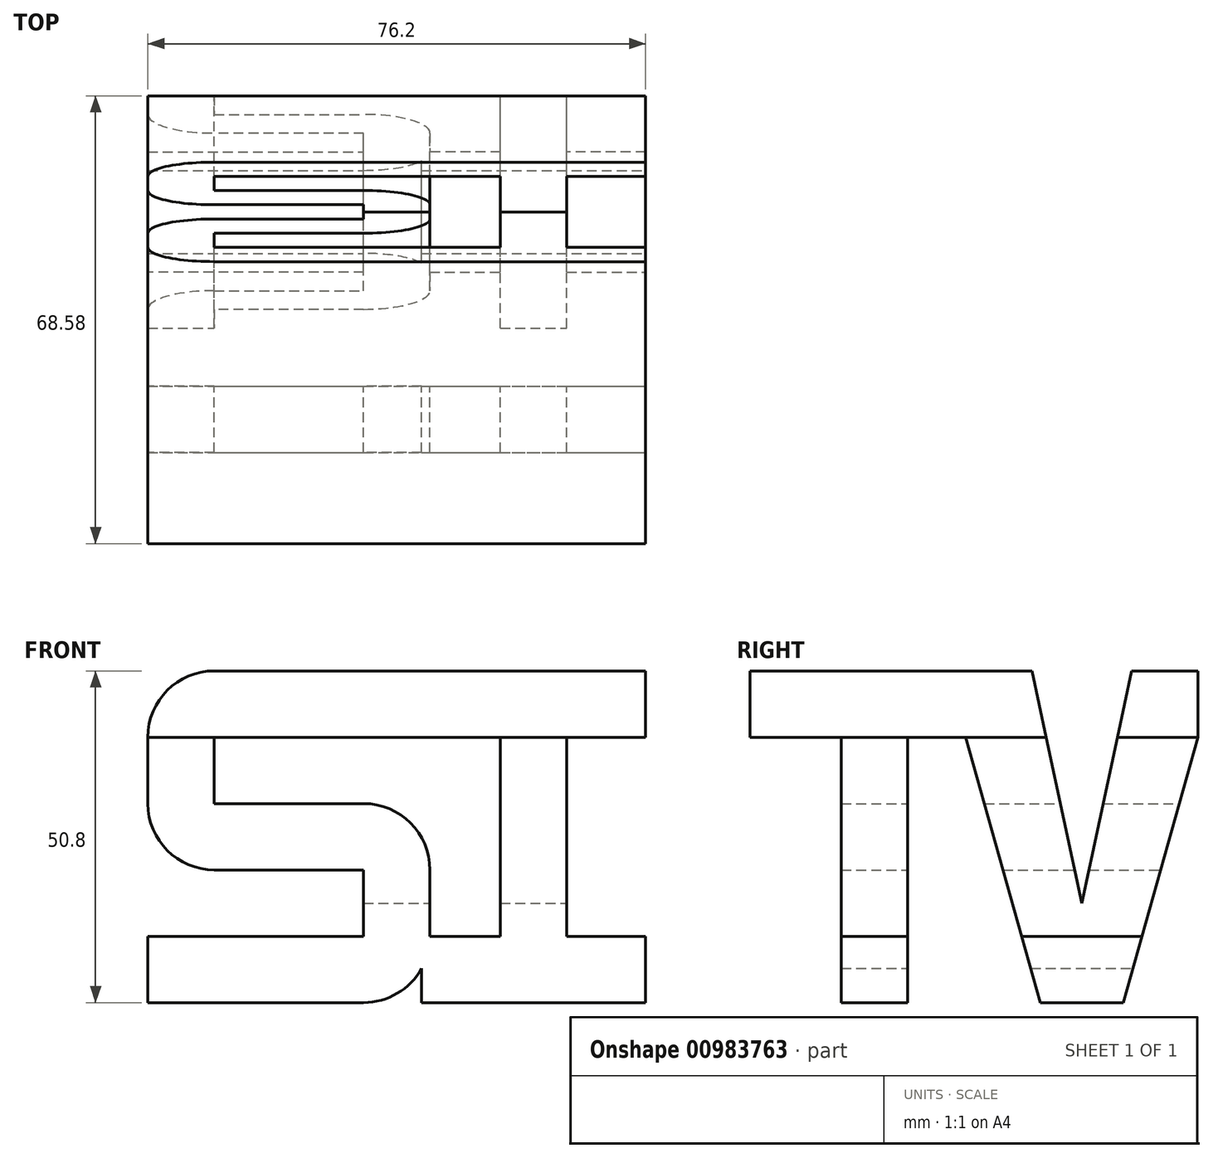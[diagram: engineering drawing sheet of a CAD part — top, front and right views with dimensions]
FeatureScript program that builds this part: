
annotation { "Feature Type Name" : "Feature", "Feature Type Description" : "" }
export const myFeature = defineFeature(function(context is Context, id is Id, definition is map)
    precondition{}
    {
        {
            var Q0;
            Q0=qCreatedBy(makeId("Front.planeOp"),FACE);
            var sketch = newSketch(context, id + "F0", { "sketchPlane" : qUnion([Q0])});
            skLineSegment(sketch, "E0", {"start": v(0, 0) * mm, "end": v(-34.29, 0) * mm});
            skLineSegment(sketch, "E1", {"start": v(0, 0) * mm, "end": v(0, 10.16) * mm});
            skLineSegment(sketch, "E2", {"start": v(0, 10.16) * mm, "end": v(-12.07, 10.16) * mm});
            skLineSegment(sketch, "E3", {"start": v(-12.07, 10.16) * mm, "end": v(-12.07, 40.64) * mm});
            skLineSegment(sketch, "E4", {"start": v(-12.07, 40.64) * mm, "end": v(0, 40.64) * mm});
            skLineSegment(sketch, "E5", {"start": v(0, 40.64) * mm, "end": v(0, 50.8) * mm});
            skLineSegment(sketch, "E6", {"start": v(0, 50.8) * mm, "end": v(-66.04, 50.8) * mm});
            skLineSegment(sketch, "E7", {"start": v(-34.29, 0) * mm, "end": v(-34.29, 10.16) * mm, "construction": true});
            skLineSegment(sketch, "E8", {"start": v(-34.29, 10.16) * mm, "end": v(-22.23, 10.16) * mm, "construction": true});
            skLineSegment(sketch, "E9", {"start": v(-12.07, 40.64) * mm, "end": v(-22.23, 40.64) * mm, "construction": true});
            skLineSegment(sketch, "E10", {"start": v(-22.23, 10.16) * mm, "end": v(-22.23, 40.64) * mm});
            skLineSegment(sketch, "E11", {"start": v(-66.04, 50.8) * mm, "end": v(-66.04, 40.64) * mm, "construction": true});
            skLineSegment(sketch, "E12", {"start": v(-66.04, 40.64) * mm, "end": v(-22.23, 40.64) * mm});
            skArc(sketch, "E13", {"start": v(-66.04, 50.8) * mm, "mid": v(-73.22, 47.82) * mm, "end": v(-76.2, 40.64) * mm});
            skLineSegment(sketch, "E14", {"start": v(-66.04, 40.64) * mm, "end": v(-66.04, 30.48) * mm});
            skLineSegment(sketch, "E15", {"start": v(-66.04, 30.48) * mm, "end": v(-43.18, 30.48) * mm});
            skLineSegment(sketch, "E16", {"start": v(-76.2, 0) * mm, "end": v(-43.18, 0) * mm});
            skLineSegment(sketch, "E17", {"start": v(-43.18, 0) * mm, "end": v(-34.29, 0) * mm, "construction": true});
            skLineSegment(sketch, "E18", {"start": v(-76.2, 0) * mm, "end": v(-76.2, 10.16) * mm});
            skLineSegment(sketch, "E19", {"start": v(-76.2, 10.16) * mm, "end": v(-43.18, 10.16) * mm});
            skLineSegment(sketch, "E20", {"start": v(-43.18, 10.16) * mm, "end": v(-43.18, 20.32) * mm});
            skLineSegment(sketch, "E21", {"start": v(-43.18, 20.32) * mm, "end": v(-66.04, 20.32) * mm});
            skArc(sketch, "E22", {"start": v(-76.2, 30.48) * mm, "mid": v(-73.22, 23.3) * mm, "end": v(-66.04, 20.32) * mm});
            skLineSegment(sketch, "E23", {"start": v(-76.2, 40.64) * mm, "end": v(-76.2, 30.48) * mm});
            skLineSegment(sketch, "E24", {"start": v(-66.04, 40.64) * mm, "end": v(-76.2, 40.64) * mm, "construction": true});
            skArc(sketch, "E25", {"start": v(-33.02, 20.32) * mm, "mid": v(-36, 27.5) * mm, "end": v(-43.18, 30.48) * mm});
            skArc(sketch, "E26", {"start": v(-43.18, 0) * mm, "mid": v(-36, 2.98) * mm, "end": v(-33.02, 10.16) * mm});
            skLineSegment(sketch, "E27", {"start": v(-33.02, 20.32) * mm, "end": v(-33.02, 10.16) * mm});
            skLineSegment(sketch, "E28", {"start": v(-43.18, 10.16) * mm, "end": v(-33.02, 10.16) * mm, "construction": true});
            skLineSegment(sketch, "E29", {"start": v(-66.04, 30.48) * mm, "end": v(-76.2, 30.48) * mm, "construction": true});
            skLineSegment(sketch, "E30", {"start": v(-66.04, 30.48) * mm, "end": v(-66.04, 20.32) * mm, "construction": true});
            skLineSegment(sketch, "E31", {"start": v(-43.18, 20.32) * mm, "end": v(-43.18, 30.48) * mm, "construction": true});
            skLineSegment(sketch, "E32", {"start": v(-43.18, 20.32) * mm, "end": v(-33.02, 20.32) * mm, "construction": true});
            skLineSegment(sketch, "E33", {"start": v(-34.29, 0) * mm, "end": v(-34.29, 5.24) * mm});
            skLineSegment(sketch, "E34", {"start": v(-22.23, 10.16) * mm, "end": v(-33.02, 10.16) * mm});
            skSolve(sketch);
        }
        {
            var Q0;
            Q0 = qSketchRegion(id + "F0", true);
            extrude(context, id + "F1", {"entities" : qUnion([Q0]), "depth" : 68.58 * mm, "offsetDistance" : 25.4 * mm});
        }
        {
            var Q0;
            Q0=qCreatedBy(makeId("Right.planeOp"),FACE);
            var sketch = newSketch(context, id + "F2", { "sketchPlane" : qUnion([Q0])});
            skLineSegment(sketch, "E35", {"start": v(0, 0) * mm, "end": v(0, 40.64) * mm, "construction": true});
            skLineSegment(sketch, "E36", {"start": v(0, 40.64) * mm, "end": v(0, 50.8) * mm});
            skLineSegment(sketch, "E37", {"start": v(0, 50.8) * mm, "end": v(-10.16, 50.8) * mm});
            skLineSegment(sketch, "E38", {"start": v(-25.4, 50.8) * mm, "end": v(-35.56, 50.8) * mm});
            skLineSegment(sketch, "E39", {"start": v(0, 40.64) * mm, "end": v(-11.43, 0) * mm});
            skLineSegment(sketch, "E40", {"start": v(-11.43, 0) * mm, "end": v(-24.13, 0) * mm});
            skLineSegment(sketch, "E41", {"start": v(-24.13, 0) * mm, "end": v(-35.56, 40.64) * mm});
            skLineSegment(sketch, "E42", {"start": v(-35.56, 40.64) * mm, "end": v(-35.56, 50.8) * mm, "construction": true});
            skLineSegment(sketch, "E43", {"start": v(-10.16, 50.8) * mm, "end": v(-17.78, 15.24) * mm});
            skLineSegment(sketch, "E44", {"start": v(0, 0) * mm, "end": v(-11.43, 0) * mm, "construction": true});
            skLineSegment(sketch, "E45", {"start": v(-24.13, 0) * mm, "end": v(-44.45, 0) * mm, "construction": true});
            skLineSegment(sketch, "E46", {"start": v(-44.45, 0) * mm, "end": v(-54.61, 0) * mm});
            skLineSegment(sketch, "E47", {"start": v(-54.61, 0) * mm, "end": v(-68.58, 0) * mm, "construction": true});
            skLineSegment(sketch, "E48", {"start": v(-68.58, 0) * mm, "end": v(-68.58, 40.64) * mm, "construction": true});
            skLineSegment(sketch, "E49", {"start": v(-68.58, 40.64) * mm, "end": v(-68.58, 50.8) * mm});
            skLineSegment(sketch, "E50", {"start": v(-54.61, 0) * mm, "end": v(-54.61, 40.64) * mm});
            skLineSegment(sketch, "E51", {"start": v(-54.61, 40.64) * mm, "end": v(-68.58, 40.64) * mm});
            skLineSegment(sketch, "E52", {"start": v(-44.45, 0) * mm, "end": v(-44.45, 40.64) * mm});
            skLineSegment(sketch, "E53", {"start": v(-44.45, 40.64) * mm, "end": v(-54.61, 40.64) * mm, "construction": true});
            skLineSegment(sketch, "E54", {"start": v(-17.78, 0) * mm, "end": v(-17.78, 15.24) * mm, "construction": true});
            skLineSegment(sketch, "E55", {"start": v(-44.45, 40.64) * mm, "end": v(-35.56, 40.64) * mm});
            skLineSegment(sketch, "E56", {"start": v(-68.58, 50.8) * mm, "end": v(-35.56, 50.8) * mm});
            skLineSegment(sketch, "E57", {"start": v(-25.4, 50.8) * mm, "end": v(-10.16, 50.8) * mm, "construction": true});
            skLineSegment(sketch, "E58", {"start": v(-17.78, 15.24) * mm, "end": v(-25.4, 50.8) * mm});
            skSolve(sketch);
        }
        {
            var Q0;
            Q0 = qSketchRegion(id + "F2", true);
            extrude(context, id + "F3", {"entities" : qUnion([Q0]), "operationType" : NewBodyOperationType.INTERSECT, "endBound" : BoundingType.THROUGH_ALL, "oppositeDirection" : true, "depth" : 25.4 * mm, "offsetDistance" : 25.4 * mm});
        }
    });
